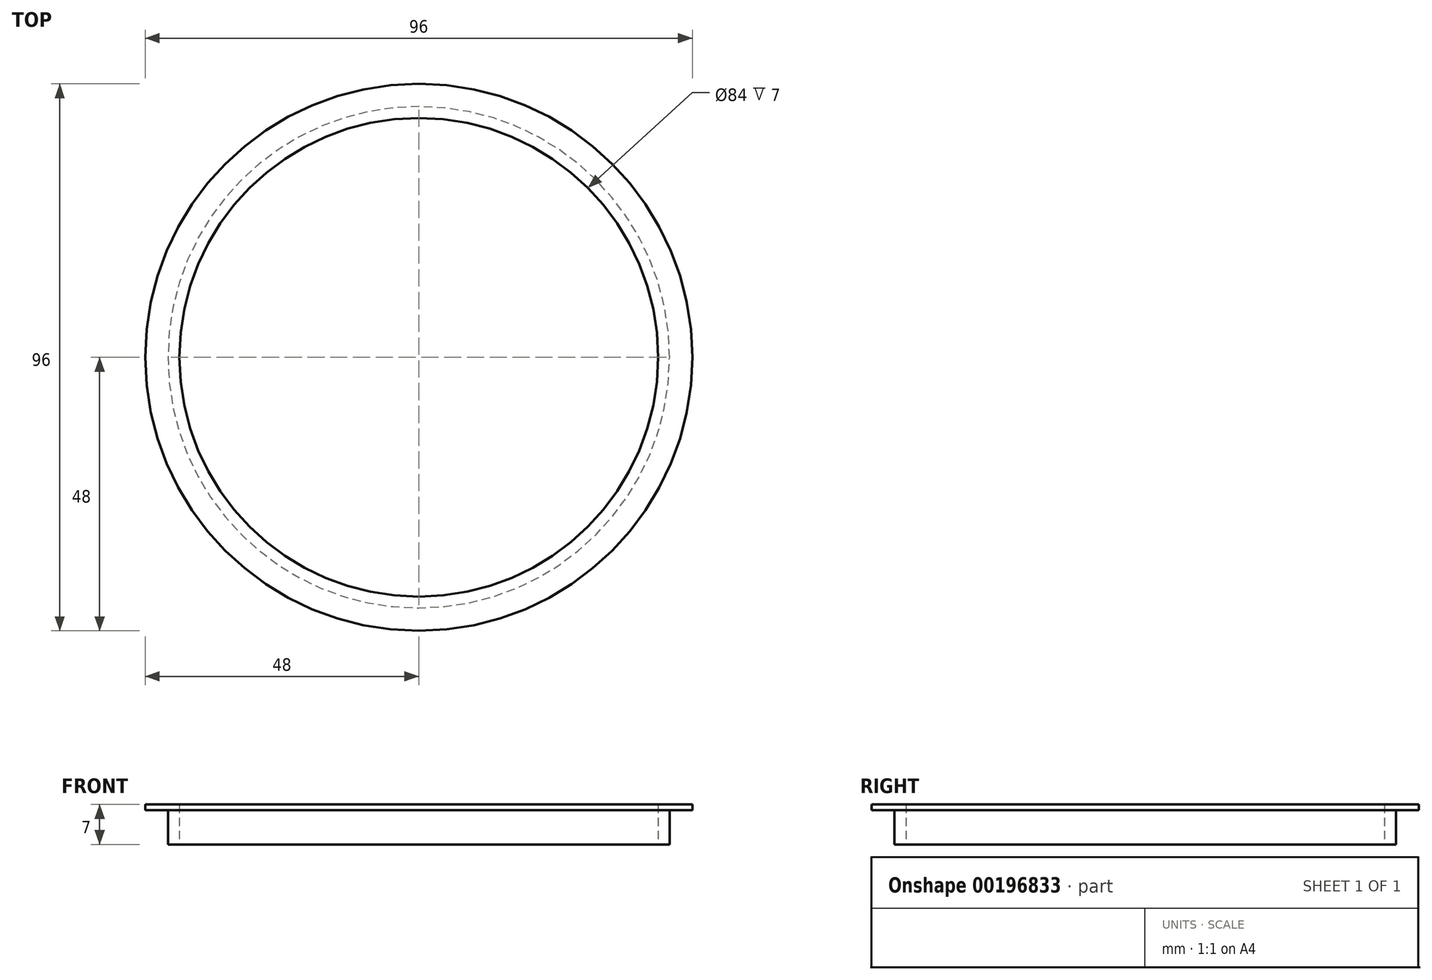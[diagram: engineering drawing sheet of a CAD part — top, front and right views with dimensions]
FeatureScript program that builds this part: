
annotation { "Feature Type Name" : "Feature", "Feature Type Description" : "" }
export const myFeature = defineFeature(function(context is Context, id is Id, definition is map)
    precondition{}
    {
        {
            var Q0;
            Q0=qCreatedBy(makeId("Top.planeOp"),FACE);
            var sketch = newSketch(context, id + "F0", { "sketchPlane" : qUnion([Q0])});
            skCircle(sketch, "E0", {"center": v(0, 0) * mm, "radius": 44 * mm});
            skCircle(sketch, "E1", {"center": v(0, 0) * mm, "radius": 42 * mm});
            skSolve(sketch);
        }
        {
            var Q0;
            Q0 = qSketchRegion(id + "F0", true);
            extrude(context, id + "F1", {"entities" : qUnion([Q0]), "depth" : 7 * mm});
        }
        {
            var Q0;
            Q0=qCreatedBy(makeId("Front.planeOp"),FACE);
            var sketch = newSketch(context, id + "F2", { "sketchPlane" : qUnion([Q0])});
            skLineSegment(sketch, "E2", {"start": v(-44, 7) * mm, "end": v(-44, 6) * mm});
            skLineSegment(sketch, "E3", {"start": v(-48, 6) * mm, "end": v(-44, 6) * mm});
            skLineSegment(sketch, "E4", {"start": v(0, 0) * mm, "end": v(0, 34.69) * mm, "construction": true});
            skLineSegment(sketch, "E5", {"start": v(-44, 7) * mm, "end": v(-48, 7) * mm});
            skLineSegment(sketch, "E6", {"start": v(-48, 7) * mm, "end": v(-48, 6) * mm});
            skSolve(sketch);
        }
        {
            var Q0;
            Q0 = qSketchRegion(id + "F2", true);
            var Q1;
            Q1=sQuery(id+"F2.wireOp",EDGE,"E4");
            revolve(context, id + "F3", {"operationType" : NewBodyOperationType.ADD, "entities" : qUnion([Q0]), "axis" : qUnion([Q1]), "revolveType" : RevolveType.FULL});
        }
    });
